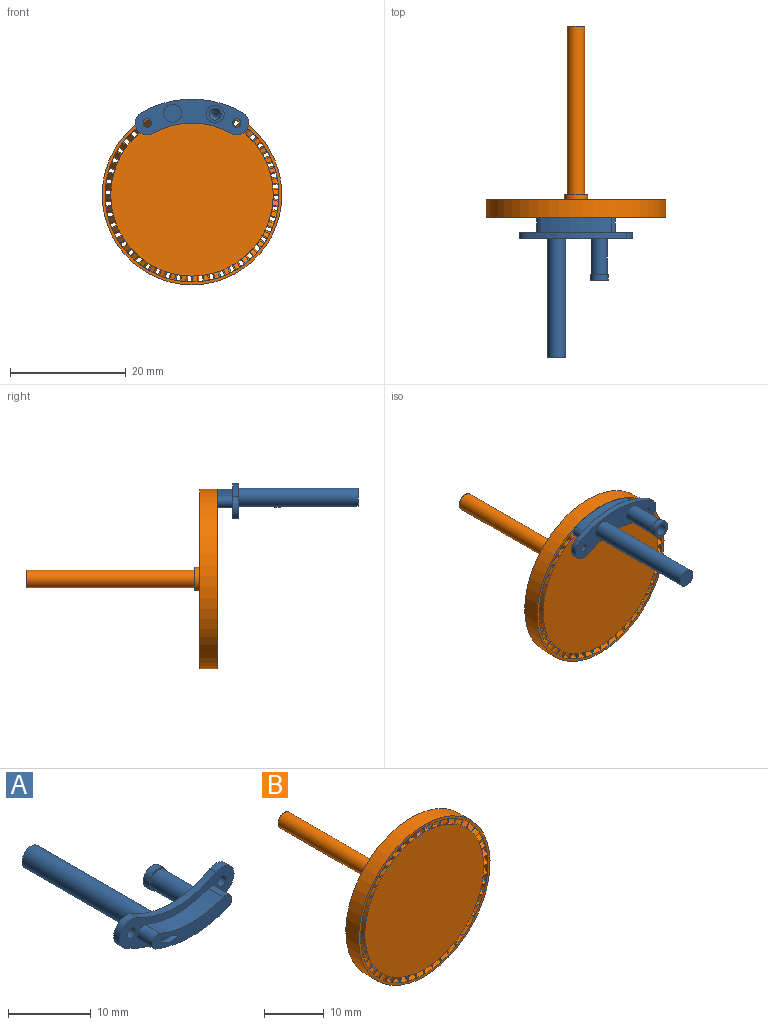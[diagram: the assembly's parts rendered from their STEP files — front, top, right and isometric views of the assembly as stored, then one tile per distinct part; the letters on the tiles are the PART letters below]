
ASSEMBLY  parts=2 mates=1
PART A: 22 faces, bbox 19.6x25x6.2 mm
  f0: cylinder r=1.54mm len=20.6mm, axis (0,-1,0), area 200mm2, adj f16,f21
  f1: cone r=0.41mm half-angle=45deg, axis (0,1,0), area 4mm2, adj f2,f5
  f2: bspline ~9.82x4.39mm, area 23.5mm2, adj f1,f12
  f3: cylinder r=1.03mm len=2.58mm, axis (0,1,0), area 8.3mm2, adj f12,f13,f19,f20
  f4: cylinder r=1.03mm len=2.58mm, axis (0,1,0), area 8.3mm2, adj f12,f13,f19,f20
  f5: cylinder r=1.03mm len=6.59mm, axis (0,-1,0), area 42.7mm2, adj f1,f17
  f6: cylinder r=1.54mm len=3.09mm, axis (0,-1,0), area 10mm2, adj f17,f18
  f7: cylinder r=1.39mm len=6.18mm, axis (0,-1,0), area 54mm2, adj f16,f18
  f8: cylinder r=0.72mm len=1.44mm, axis (0,1,0), area 4.7mm2, adj f13,f16
  f9: cylinder r=0.72mm len=1.44mm, axis (0,1,0), area 4.7mm2, adj f13,f16
  f10: cylinder r=13.39mm len=13.39mm, axis (0,-1,0), area 14.4mm2, adj f13,f14,f15,f16
  f11: cylinder r=17.51mm len=17.51mm, axis (0,-1,0), area 18.9mm2, adj f13,f14,f15,f16
  f12: plane 13.64x3.19mm, normal (0,-1,0), area 25.9mm2, adj f2,f3,f4,f19,f20
  f13: plane 19.57x6.19mm, normal (0,-1,0), area 48.9mm2, adj f3,f4,f8,f9,f10,f11,f14,f15
  f14: cylinder r=2.06mm len=3.84mm, axis (0,-1,0), area 6.7mm2, adj f10,f11,f13,f16
  f15: cylinder r=2.06mm len=3.84mm, axis (0,-1,0), area 6.7mm2, adj f10,f11,f13,f16
  f16: plane 19.57x6.19mm, normal (0,1,0), area 63.2mm2, adj f0,f7,f8,f9,f10,f11,f14,f15
  f17: plane 3.09x3.09mm, normal (0,1,0), area 4.2mm2, adj f5,f6
  f18: plane 3.09x3.09mm, normal (0,-1,0), area 1.4mm2, adj f6,f7
  f19: cylinder r=16.48mm len=12.35mm, axis (0,1,0), area 32.6mm2, adj f3,f4,f12,f13
  f20: cylinder r=14.42mm len=10.8mm, axis (0,1,0), area 28.5mm2, adj f3,f4,f12,f13
  f21: plane 3.09x3.09mm, normal (0,1,0), area 7.5mm2, adj f0
PART B: 295 faces, bbox 31x33x31 mm
  f0: cylinder r=2.02mm len=3mm, axis (0,0,-1), area 3.4mm2, adj f192,f240,f241,f289
  f1: plane 1.03x0.8mm, normal (-0.71,0.7,0), area 1.1mm2, adj f2,f239,f240,f242
  f2: cylinder r=1mm len=1.4mm, axis (0,0,-1), area 1.6mm2, adj f1,f3,f239,f242
  f3: plane 1.03x0.8mm, normal (-0.72,-0.7,0), area 1.1mm2, adj f2,f239,f241,f242
  f4: cylinder r=2.02mm len=3mm, axis (0.13,0,-0.99), area 3.4mm2, adj f239,f240,f241,f242
  f5: plane 1.12x0.91mm, normal (-0.7,0.7,-0.09), area 1.1mm2, adj f6,f238,f240,f243
  f6: cylinder r=1mm len=1.4mm, axis (0.13,0,-0.99), area 1.6mm2, adj f5,f7,f238,f243
  f7: plane 1.12x0.9mm, normal (-0.71,-0.7,-0.09), area 1.1mm2, adj f6,f238,f241,f243
  f8: cylinder r=2.02mm len=3mm, axis (0.26,0,-0.97), area 3.4mm2, adj f238,f240,f241,f243
  f9: plane 1.2x1.01mm, normal (-0.69,0.7,-0.18), area 1.1mm2, adj f10,f237,f240,f244
  f10: cylinder r=1mm len=1.4mm, axis (0.26,0,-0.97), area 1.6mm2, adj f9,f11,f237,f244
  f11: plane 1.19x1.01mm, normal (-0.69,-0.7,-0.19), area 1.1mm2, adj f10,f237,f241,f244
  f12: cylinder r=2.02mm len=3mm, axis (0.38,0,-0.92), area 3.4mm2, adj f237,f240,f241,f244
  f13: plane 1.25x1.1mm, normal (-0.66,0.7,-0.27), area 1.1mm2, adj f14,f236,f240,f245
  f14: cylinder r=1mm len=1.4mm, axis (0.38,0,-0.92), area 1.6mm2, adj f13,f15,f236,f245
  f15: plane 1.25x1.1mm, normal (-0.66,-0.7,-0.27), area 1.1mm2, adj f14,f236,f241,f245
  f16: cylinder r=2.02mm len=3mm, axis (0.5,0,-0.87), area 3.4mm2, adj f236,f240,f241,f245
  f17: plane 1.28x1.17mm, normal (-0.62,0.7,-0.36), area 1.1mm2, adj f18,f235,f240,f246
  f18: cylinder r=1mm len=1.4mm, axis (0.5,0,-0.87), area 1.6mm2, adj f17,f19,f235,f246
  f19: plane 1.28x1.16mm, normal (-0.62,-0.7,-0.36), area 1.1mm2, adj f18,f235,f241,f246
  f20: cylinder r=2.02mm len=3mm, axis (0.61,0,-0.79), area 3.4mm2, adj f235,f240,f241,f246
  f21: plane 1.29x1.22mm, normal (-0.56,0.7,-0.43), area 1.1mm2, adj f22,f234,f240,f247
  f22: cylinder r=1mm len=1.4mm, axis (0.61,0,-0.79), area 1.6mm2, adj f21,f23,f234,f247
  f23: plane 1.29x1.21mm, normal (-0.57,-0.7,-0.44), area 1.1mm2, adj f22,f234,f241,f247
  f24: cylinder r=2.02mm len=3mm, axis (0.71,0,-0.71), area 3.4mm2, adj f234,f240,f241,f247
  f25: plane 1.28x1.25mm, normal (-0.5,0.7,-0.5), area 1.1mm2, adj f26,f233,f240,f248
  f26: cylinder r=1mm len=1.4mm, axis (0.71,0,-0.71), area 1.6mm2, adj f25,f27,f233,f248
  f27: plane 1.28x1.24mm, normal (-0.51,-0.7,-0.51), area 1.1mm2, adj f26,f233,f241,f248
  f28: cylinder r=2.02mm len=3mm, axis (0.79,0,-0.61), area 3.4mm2, adj f233,f240,f241,f248
  f29: plane 1.25x1.25mm, normal (-0.43,0.7,-0.56), area 1.1mm2, adj f30,f232,f240,f249
  f30: cylinder r=1mm len=1.4mm, axis (0.79,0,-0.61), area 1.6mm2, adj f29,f31,f232,f249
  f31: plane 1.25x1.25mm, normal (-0.44,-0.7,-0.57), area 1.1mm2, adj f30,f232,f241,f249
  f32: cylinder r=2.02mm len=3mm, axis (0.87,0,-0.5), area 3.4mm2, adj f232,f240,f241,f249
  f33: plane 1.24x1.2mm, normal (-0.36,0.7,-0.62), area 1.1mm2, adj f34,f231,f240,f250
  f34: cylinder r=1mm len=1.4mm, axis (0.87,0,-0.5), area 1.6mm2, adj f33,f35,f231,f250
  f35: plane 1.24x1.19mm, normal (-0.36,-0.7,-0.62), area 1.1mm2, adj f34,f231,f241,f250
  f36: cylinder r=2.02mm len=3mm, axis (0.92,0,-0.38), area 3.4mm2, adj f231,f240,f241,f250
  f37: plane 1.2x1.12mm, normal (-0.27,0.7,-0.66), area 1.1mm2, adj f38,f230,f240,f251
  f38: cylinder r=1mm len=1.4mm, axis (0.92,0,-0.38), area 1.6mm2, adj f37,f39,f230,f251
  f39: plane 1.2x1.12mm, normal (-0.27,-0.7,-0.66), area 1.1mm2, adj f38,f230,f241,f251
  f40: cylinder r=2.02mm len=3mm, axis (0.97,0,-0.26), area 3.4mm2, adj f230,f240,f241,f251
  f41: plane 1.15x1.03mm, normal (-0.18,0.7,-0.69), area 1.1mm2, adj f42,f229,f240,f252
  f42: cylinder r=1mm len=1.4mm, axis (0.97,0,-0.26), area 1.6mm2, adj f41,f43,f229,f252
  f43: plane 1.14x1.02mm, normal (-0.19,-0.7,-0.69), area 1.1mm2, adj f42,f229,f241,f252
  f44: cylinder r=2.02mm len=3mm, axis (0.99,0,-0.13), area 3.4mm2, adj f229,f240,f241,f252
  f45: plane 1.07x0.92mm, normal (-0.09,0.7,-0.7), area 1.1mm2, adj f46,f228,f240,f253
  f46: cylinder r=1mm len=1.4mm, axis (0.99,0,-0.13), area 1.6mm2, adj f45,f47,f228,f253
  f47: plane 1.07x0.91mm, normal (-0.09,-0.7,-0.71), area 1.1mm2, adj f46,f228,f241,f253
  f48: cylinder r=2.02mm len=3mm, axis (1,0,0), area 3.4mm2, adj f228,f240,f241,f253
  f49: plane 1.03x0.8mm, normal (0,0.7,-0.71), area 1.1mm2, adj f50,f227,f240,f254
  f50: cylinder r=1mm len=1.4mm, axis (1,0,0), area 1.6mm2, adj f49,f51,f227,f254
  f51: plane 1.03x0.8mm, normal (0,-0.7,-0.72), area 1.1mm2, adj f50,f227,f241,f254
  f52: cylinder r=2.02mm len=3mm, axis (0.99,0,0.13), area 3.4mm2, adj f227,f240,f241,f254
  f53: plane 1.12x0.91mm, normal (0.09,0.7,-0.7), area 1.1mm2, adj f54,f226,f240,f255
  f54: cylinder r=1mm len=1.4mm, axis (0.99,0,0.13), area 1.6mm2, adj f53,f55,f226,f255
  f55: plane 1.12x0.9mm, normal (0.09,-0.7,-0.71), area 1.1mm2, adj f54,f226,f241,f255
  f56: cylinder r=2.02mm len=3mm, axis (0.97,0,0.26), area 3.4mm2, adj f226,f240,f241,f255
  f57: plane 1.2x1.01mm, normal (0.18,0.7,-0.69), area 1.1mm2, adj f58,f225,f240,f256
  f58: cylinder r=1mm len=1.4mm, axis (0.97,0,0.26), area 1.6mm2, adj f57,f59,f225,f256
  f59: plane 1.19x1.01mm, normal (0.19,-0.7,-0.69), area 1.1mm2, adj f58,f225,f241,f256
  f60: cylinder r=2.02mm len=3mm, axis (0.92,0,0.38), area 3.4mm2, adj f225,f240,f241,f256
  f61: plane 1.25x1.1mm, normal (0.27,0.7,-0.66), area 1.1mm2, adj f62,f224,f240,f257
  f62: cylinder r=1mm len=1.4mm, axis (0.92,0,0.38), area 1.6mm2, adj f61,f63,f224,f257
  f63: plane 1.25x1.1mm, normal (0.27,-0.7,-0.66), area 1.1mm2, adj f62,f224,f241,f257
  f64: cylinder r=2.02mm len=3mm, axis (0.87,0,0.5), area 3.4mm2, adj f224,f240,f241,f257
  f65: plane 1.28x1.17mm, normal (0.36,0.7,-0.62), area 1.1mm2, adj f66,f223,f240,f258
  f66: cylinder r=1mm len=1.4mm, axis (0.87,0,0.5), area 1.6mm2, adj f65,f67,f223,f258
  f67: plane 1.28x1.16mm, normal (0.36,-0.7,-0.62), area 1.1mm2, adj f66,f223,f241,f258
  f68: cylinder r=2.02mm len=3mm, axis (0.79,0,0.61), area 3.4mm2, adj f223,f240,f241,f258
  f69: plane 1.29x1.22mm, normal (0.43,0.7,-0.56), area 1.1mm2, adj f70,f222,f240,f259
  f70: cylinder r=1mm len=1.4mm, axis (0.79,0,0.61), area 1.6mm2, adj f69,f71,f222,f259
  f71: plane 1.29x1.21mm, normal (0.44,-0.7,-0.57), area 1.1mm2, adj f70,f222,f241,f259
  f72: cylinder r=2.02mm len=3mm, axis (0.71,0,0.71), area 3.4mm2, adj f222,f240,f241,f259
  f73: plane 1.28x1.25mm, normal (0.5,0.7,-0.5), area 1.1mm2, adj f74,f221,f240,f260
  f74: cylinder r=1mm len=1.4mm, axis (0.71,0,0.71), area 1.6mm2, adj f73,f75,f221,f260
  f75: plane 1.28x1.24mm, normal (0.51,-0.7,-0.51), area 1.1mm2, adj f74,f221,f241,f260
  f76: cylinder r=2.02mm len=3mm, axis (0.61,0,0.79), area 3.4mm2, adj f221,f240,f241,f260
  f77: plane 1.25x1.25mm, normal (0.56,0.7,-0.43), area 1.1mm2, adj f78,f220,f240,f261
  f78: cylinder r=1mm len=1.4mm, axis (0.61,0,0.79), area 1.6mm2, adj f77,f79,f220,f261
  f79: plane 1.25x1.25mm, normal (0.57,-0.7,-0.44), area 1.1mm2, adj f78,f220,f241,f261
  f80: cylinder r=2.02mm len=3mm, axis (0.5,0,0.87), area 3.4mm2, adj f220,f240,f241,f261
  f81: plane 1.24x1.2mm, normal (0.62,0.7,-0.36), area 1.1mm2, adj f82,f219,f240,f262
  f82: cylinder r=1mm len=1.4mm, axis (0.5,0,0.87), area 1.6mm2, adj f81,f83,f219,f262
  f83: plane 1.24x1.19mm, normal (0.62,-0.7,-0.36), area 1.1mm2, adj f82,f219,f241,f262
  f84: cylinder r=2.02mm len=3mm, axis (0.38,0,0.92), area 3.4mm2, adj f219,f240,f241,f262
  f85: plane 1.2x1.12mm, normal (0.66,0.7,-0.27), area 1.1mm2, adj f86,f218,f240,f263
  f86: cylinder r=1mm len=1.4mm, axis (0.38,0,0.92), area 1.6mm2, adj f85,f87,f218,f263
  f87: plane 1.2x1.12mm, normal (0.66,-0.7,-0.27), area 1.1mm2, adj f86,f218,f241,f263
  f88: cylinder r=2.02mm len=3mm, axis (0.26,0,0.97), area 3.4mm2, adj f218,f240,f241,f263
  f89: plane 1.15x1.03mm, normal (0.69,0.7,-0.18), area 1.1mm2, adj f90,f217,f240,f264
  f90: cylinder r=1mm len=1.4mm, axis (0.26,0,0.97), area 1.6mm2, adj f89,f91,f217,f264
  f91: plane 1.14x1.02mm, normal (0.69,-0.7,-0.19), area 1.1mm2, adj f90,f217,f241,f264
  f92: cylinder r=2.02mm len=3mm, axis (0.13,0,0.99), area 3.4mm2, adj f217,f240,f241,f264
  f93: plane 1.07x0.92mm, normal (0.7,0.7,-0.09), area 1.1mm2, adj f94,f216,f240,f265
  f94: cylinder r=1mm len=1.4mm, axis (0.13,0,0.99), area 1.6mm2, adj f93,f95,f216,f265
  f95: plane 1.07x0.91mm, normal (0.71,-0.7,-0.09), area 1.1mm2, adj f94,f216,f241,f265
  f96: cylinder r=2.02mm len=3mm, axis (0,0,1), area 3.4mm2, adj f216,f240,f241,f265
  f97: plane 1.03x0.8mm, normal (0.71,0.7,0), area 1.1mm2, adj f98,f215,f240,f266
  f98: cylinder r=1mm len=1.4mm, axis (0,0,1), area 1.6mm2, adj f97,f99,f215,f266
  f99: plane 1.03x0.8mm, normal (0.72,-0.7,0), area 1.1mm2, adj f98,f215,f241,f266
  f100: cylinder r=2.02mm len=3mm, axis (-0.13,0,0.99), area 3.4mm2, adj f215,f240,f241,f266
  f101: plane 1.12x0.91mm, normal (0.7,0.7,0.09), area 1.1mm2, adj f102,f214,f240,f267
  f102: cylinder r=1mm len=1.4mm, axis (-0.13,0,0.99), area 1.6mm2, adj f101,f103,f214,f267
  f103: plane 1.12x0.9mm, normal (0.71,-0.7,0.09), area 1.1mm2, adj f102,f214,f241,f267
  f104: cylinder r=2.02mm len=3mm, axis (-0.26,0,0.97), area 3.4mm2, adj f214,f240,f241,f267
  f105: plane 1.2x1.01mm, normal (0.69,0.7,0.18), area 1.1mm2, adj f106,f213,f240,f268
  f106: cylinder r=1mm len=1.4mm, axis (-0.26,0,0.97), area 1.6mm2, adj f105,f107,f213,f268
  f107: plane 1.19x1.01mm, normal (0.69,-0.7,0.19), area 1.1mm2, adj f106,f213,f241,f268
  f108: cylinder r=2.02mm len=3mm, axis (-0.38,0,0.92), area 3.4mm2, adj f213,f240,f241,f268
  f109: plane 1.25x1.1mm, normal (0.66,0.7,0.27), area 1.1mm2, adj f110,f212,f240,f269
  f110: cylinder r=1mm len=1.4mm, axis (-0.38,0,0.92), area 1.6mm2, adj f109,f111,f212,f269
  f111: plane 1.25x1.1mm, normal (0.66,-0.7,0.27), area 1.1mm2, adj f110,f212,f241,f269
  f112: cylinder r=2.02mm len=3mm, axis (-0.5,0,0.87), area 3.4mm2, adj f212,f240,f241,f269
  f113: plane 1.28x1.17mm, normal (0.62,0.7,0.36), area 1.1mm2, adj f114,f211,f240,f270
  f114: cylinder r=1mm len=1.4mm, axis (-0.5,0,0.87), area 1.6mm2, adj f113,f115,f211,f270
  f115: plane 1.28x1.16mm, normal (0.62,-0.7,0.36), area 1.1mm2, adj f114,f211,f241,f270
  f116: cylinder r=2.02mm len=3mm, axis (-0.61,0,0.79), area 3.4mm2, adj f211,f240,f241,f270
  f117: plane 1.29x1.22mm, normal (0.56,0.7,0.43), area 1.1mm2, adj f118,f210,f240,f271
  f118: cylinder r=1mm len=1.4mm, axis (-0.61,0,0.79), area 1.6mm2, adj f117,f119,f210,f271
  f119: plane 1.29x1.21mm, normal (0.57,-0.7,0.44), area 1.1mm2, adj f118,f210,f241,f271
  f120: cylinder r=2.02mm len=3mm, axis (-0.71,0,0.71), area 3.4mm2, adj f210,f240,f241,f271
  f121: plane 1.28x1.25mm, normal (0.5,0.7,0.5), area 1.1mm2, adj f122,f209,f240,f272
  f122: cylinder r=1mm len=1.4mm, axis (-0.71,0,0.71), area 1.6mm2, adj f121,f123,f209,f272
  f123: plane 1.28x1.24mm, normal (0.51,-0.7,0.51), area 1.1mm2, adj f122,f209,f241,f272
  f124: cylinder r=2.02mm len=3mm, axis (-0.79,0,0.61), area 3.4mm2, adj f209,f240,f241,f272
  f125: plane 1.25x1.25mm, normal (0.43,0.7,0.56), area 1.1mm2, adj f126,f208,f240,f273
  f126: cylinder r=1mm len=1.4mm, axis (-0.79,0,0.61), area 1.6mm2, adj f125,f127,f208,f273
  f127: plane 1.25x1.25mm, normal (0.44,-0.7,0.57), area 1.1mm2, adj f126,f208,f241,f273
  f128: cylinder r=2.02mm len=3mm, axis (-0.87,0,0.5), area 3.4mm2, adj f208,f240,f241,f273
  f129: plane 1.24x1.2mm, normal (0.36,0.7,0.62), area 1.1mm2, adj f130,f207,f240,f274
  f130: cylinder r=1mm len=1.4mm, axis (-0.87,0,0.5), area 1.6mm2, adj f129,f131,f207,f274
  f131: plane 1.24x1.19mm, normal (0.36,-0.7,0.62), area 1.1mm2, adj f130,f207,f241,f274
  f132: cylinder r=2.02mm len=3mm, axis (-0.92,0,0.38), area 3.4mm2, adj f207,f240,f241,f274
  f133: plane 1.2x1.12mm, normal (0.27,0.7,0.66), area 1.1mm2, adj f134,f206,f240,f275
  f134: cylinder r=1mm len=1.4mm, axis (-0.92,0,0.38), area 1.6mm2, adj f133,f135,f206,f275
  f135: plane 1.2x1.12mm, normal (0.27,-0.7,0.66), area 1.1mm2, adj f134,f206,f241,f275
  f136: cylinder r=2.02mm len=3mm, axis (-0.97,0,0.26), area 3.4mm2, adj f206,f240,f241,f275
  f137: plane 1.15x1.03mm, normal (0.18,0.7,0.69), area 1.1mm2, adj f138,f205,f240,f276
  f138: cylinder r=1mm len=1.4mm, axis (-0.97,0,0.26), area 1.6mm2, adj f137,f139,f205,f276
  f139: plane 1.14x1.02mm, normal (0.19,-0.7,0.69), area 1.1mm2, adj f138,f205,f241,f276
  f140: cylinder r=2.02mm len=3mm, axis (-0.99,0,0.13), area 3.4mm2, adj f205,f240,f241,f276
  f141: plane 1.07x0.92mm, normal (0.09,0.7,0.7), area 1.1mm2, adj f142,f204,f240,f277
  f142: cylinder r=1mm len=1.4mm, axis (-0.99,0,0.13), area 1.6mm2, adj f141,f143,f204,f277
  f143: plane 1.07x0.91mm, normal (0.09,-0.7,0.71), area 1.1mm2, adj f142,f204,f241,f277
  f144: cylinder r=2.02mm len=3mm, axis (-1,0,0), area 3.4mm2, adj f204,f240,f241,f277
  f145: plane 1.03x0.8mm, normal (0,0.7,0.71), area 1.1mm2, adj f146,f203,f240,f278
  f146: cylinder r=1mm len=1.4mm, axis (-1,0,0), area 1.6mm2, adj f145,f147,f203,f278
  f147: plane 1.03x0.8mm, normal (0,-0.7,0.72), area 1.1mm2, adj f146,f203,f241,f278
  f148: cylinder r=2.02mm len=3mm, axis (-0.99,0,-0.13), area 3.4mm2, adj f203,f240,f241,f278
  f149: plane 1.12x0.91mm, normal (-0.09,0.7,0.7), area 1.1mm2, adj f150,f202,f240,f279
  f150: cylinder r=1mm len=1.4mm, axis (-0.99,0,-0.13), area 1.6mm2, adj f149,f151,f202,f279
  f151: plane 1.12x0.9mm, normal (-0.09,-0.7,0.71), area 1.1mm2, adj f150,f202,f241,f279
  f152: cylinder r=2.02mm len=3mm, axis (-0.97,0,-0.26), area 3.4mm2, adj f202,f240,f241,f279
  f153: plane 1.2x1.01mm, normal (-0.18,0.7,0.69), area 1.1mm2, adj f154,f201,f240,f280
  f154: cylinder r=1mm len=1.4mm, axis (-0.97,0,-0.26), area 1.6mm2, adj f153,f155,f201,f280
  f155: plane 1.19x1.01mm, normal (-0.19,-0.7,0.69), area 1.1mm2, adj f154,f201,f241,f280
  f156: cylinder r=2.02mm len=3mm, axis (-0.92,0,-0.38), area 3.4mm2, adj f201,f240,f241,f280
  f157: plane 1.25x1.1mm, normal (-0.27,0.7,0.66), area 1.1mm2, adj f158,f200,f240,f281
  f158: cylinder r=1mm len=1.4mm, axis (-0.92,0,-0.38), area 1.6mm2, adj f157,f159,f200,f281
  f159: plane 1.25x1.1mm, normal (-0.27,-0.7,0.66), area 1.1mm2, adj f158,f200,f241,f281
  f160: cylinder r=2.02mm len=3mm, axis (-0.87,0,-0.5), area 3.4mm2, adj f200,f240,f241,f281
  f161: plane 1.28x1.17mm, normal (-0.36,0.7,0.62), area 1.1mm2, adj f162,f199,f240,f282
  f162: cylinder r=1mm len=1.4mm, axis (-0.87,0,-0.5), area 1.6mm2, adj f161,f163,f199,f282
  f163: plane 1.28x1.16mm, normal (-0.36,-0.7,0.62), area 1.1mm2, adj f162,f199,f241,f282
  f164: cylinder r=2.02mm len=3mm, axis (-0.79,0,-0.61), area 3.4mm2, adj f199,f240,f241,f282
  f165: plane 1.29x1.22mm, normal (-0.43,0.7,0.56), area 1.1mm2, adj f166,f198,f240,f283
  f166: cylinder r=1mm len=1.4mm, axis (-0.79,0,-0.61), area 1.6mm2, adj f165,f167,f198,f283
  f167: plane 1.29x1.21mm, normal (-0.44,-0.7,0.57), area 1.1mm2, adj f166,f198,f241,f283
  f168: cylinder r=2.02mm len=3mm, axis (-0.71,0,-0.71), area 3.4mm2, adj f198,f240,f241,f283
  f169: plane 1.28x1.25mm, normal (-0.5,0.7,0.5), area 1.1mm2, adj f170,f197,f240,f284
  f170: cylinder r=1mm len=1.4mm, axis (-0.71,0,-0.71), area 1.6mm2, adj f169,f171,f197,f284
  f171: plane 1.28x1.24mm, normal (-0.51,-0.7,0.51), area 1.1mm2, adj f170,f197,f241,f284
  f172: cylinder r=2.02mm len=3mm, axis (-0.61,0,-0.79), area 3.4mm2, adj f197,f240,f241,f284
  f173: plane 1.25x1.25mm, normal (-0.56,0.7,0.43), area 1.1mm2, adj f174,f196,f240,f285
  f174: cylinder r=1mm len=1.4mm, axis (-0.61,0,-0.79), area 1.6mm2, adj f173,f175,f196,f285
  f175: plane 1.25x1.25mm, normal (-0.57,-0.7,0.44), area 1.1mm2, adj f174,f196,f241,f285
  f176: cylinder r=2.02mm len=3mm, axis (-0.5,0,-0.87), area 3.4mm2, adj f196,f240,f241,f285
  f177: plane 1.24x1.2mm, normal (-0.62,0.7,0.36), area 1.1mm2, adj f178,f195,f240,f286
  f178: cylinder r=1mm len=1.4mm, axis (-0.5,0,-0.87), area 1.6mm2, adj f177,f179,f195,f286
  f179: plane 1.24x1.19mm, normal (-0.62,-0.7,0.36), area 1.1mm2, adj f178,f195,f241,f286
  f180: cylinder r=2.02mm len=3mm, axis (-0.38,0,-0.92), area 3.4mm2, adj f195,f240,f241,f286
  f181: plane 1.2x1.12mm, normal (-0.66,0.7,0.27), area 1.1mm2, adj f182,f194,f240,f287
  f182: cylinder r=1mm len=1.4mm, axis (-0.38,0,-0.92), area 1.6mm2, adj f181,f183,f194,f287
  f183: plane 1.2x1.12mm, normal (-0.66,-0.7,0.27), area 1.1mm2, adj f182,f194,f241,f287
  f184: cylinder r=2.02mm len=3mm, axis (-0.26,0,-0.97), area 3.4mm2, adj f194,f240,f241,f287
  f185: plane 1.15x1.03mm, normal (-0.69,0.7,0.18), area 1.1mm2, adj f186,f193,f240,f288
  f186: cylinder r=1mm len=1.4mm, axis (-0.26,0,-0.97), area 1.6mm2, adj f185,f187,f193,f288
  f187: plane 1.14x1.02mm, normal (-0.69,-0.7,0.19), area 1.1mm2, adj f186,f193,f241,f288
  f188: cylinder r=2.02mm len=3mm, axis (-0.13,0,-0.99), area 3.4mm2, adj f193,f240,f241,f288
  f189: plane 1.07x0.92mm, normal (-0.7,0.7,0.09), area 1.1mm2, adj f190,f192,f240,f289
  f190: cylinder r=1mm len=1.4mm, axis (-0.13,0,-0.99), area 1.6mm2, adj f189,f191,f192,f289
  f191: plane 1.07x0.91mm, normal (-0.71,-0.7,0.09), area 1.1mm2, adj f190,f192,f241,f289
  f192: cylinder r=14mm len=3mm, axis (0,-1,0), area 4.4mm2, adj f0,f189,f190,f191,f240,f241
  f193: cylinder r=14mm len=3mm, axis (0,-1,0), area 4.4mm2, adj f185,f186,f187,f188,f240,f241
  f194: cylinder r=14mm len=3mm, axis (0,-1,0), area 4.4mm2, adj f181,f182,f183,f184,f240,f241
  f195: cylinder r=14mm len=3mm, axis (0,-1,0), area 4.4mm2, adj f177,f178,f179,f180,f240,f241
  f196: cylinder r=14mm len=3mm, axis (0,-1,0), area 4.4mm2, adj f173,f174,f175,f176,f240,f241
  f197: cylinder r=14mm len=3mm, axis (0,-1,0), area 4.4mm2, adj f169,f170,f171,f172,f240,f241
  f198: cylinder r=14mm len=3mm, axis (0,-1,0), area 4.4mm2, adj f165,f166,f167,f168,f240,f241
  f199: cylinder r=14mm len=3mm, axis (0,-1,0), area 4.4mm2, adj f161,f162,f163,f164,f240,f241
  f200: cylinder r=14mm len=3mm, axis (0,-1,0), area 4.4mm2, adj f157,f158,f159,f160,f240,f241
  f201: cylinder r=14mm len=3mm, axis (0,-1,0), area 4.4mm2, adj f153,f154,f155,f156,f240,f241
  f202: cylinder r=14mm len=3mm, axis (0,-1,0), area 4.4mm2, adj f149,f150,f151,f152,f240,f241
  f203: cylinder r=14mm len=3mm, axis (0,-1,0), area 4.4mm2, adj f145,f146,f147,f148,f240,f241
  f204: cylinder r=14mm len=3mm, axis (0,-1,0), area 4.4mm2, adj f141,f142,f143,f144,f240,f241
  f205: cylinder r=14mm len=3mm, axis (0,-1,0), area 4.4mm2, adj f137,f138,f139,f140,f240,f241
  f206: cylinder r=14mm len=3mm, axis (0,-1,0), area 4.4mm2, adj f133,f134,f135,f136,f240,f241
  f207: cylinder r=14mm len=3mm, axis (0,-1,0), area 4.4mm2, adj f129,f130,f131,f132,f240,f241
  f208: cylinder r=14mm len=3mm, axis (0,-1,0), area 4.4mm2, adj f125,f126,f127,f128,f240,f241
  f209: cylinder r=14mm len=3mm, axis (0,-1,0), area 4.4mm2, adj f121,f122,f123,f124,f240,f241
  f210: cylinder r=14mm len=3mm, axis (0,-1,0), area 4.4mm2, adj f117,f118,f119,f120,f240,f241
  f211: cylinder r=14mm len=3mm, axis (0,-1,0), area 4.4mm2, adj f113,f114,f115,f116,f240,f241
  f212: cylinder r=14mm len=3mm, axis (0,-1,0), area 4.4mm2, adj f109,f110,f111,f112,f240,f241
  f213: cylinder r=14mm len=3mm, axis (0,-1,0), area 4.4mm2, adj f105,f106,f107,f108,f240,f241
  f214: cylinder r=14mm len=3mm, axis (0,-1,0), area 4.4mm2, adj f101,f102,f103,f104,f240,f241
  f215: cylinder r=14mm len=3mm, axis (0,-1,0), area 4.4mm2, adj f97,f98,f99,f100,f240,f241
  f216: cylinder r=14mm len=3mm, axis (0,-1,0), area 4.4mm2, adj f93,f94,f95,f96,f240,f241
  f217: cylinder r=14mm len=3mm, axis (0,-1,0), area 4.4mm2, adj f89,f90,f91,f92,f240,f241
  f218: cylinder r=14mm len=3mm, axis (0,-1,0), area 4.4mm2, adj f85,f86,f87,f88,f240,f241
  f219: cylinder r=14mm len=3mm, axis (0,-1,0), area 4.4mm2, adj f81,f82,f83,f84,f240,f241
  f220: cylinder r=14mm len=3mm, axis (0,-1,0), area 4.4mm2, adj f77,f78,f79,f80,f240,f241
  f221: cylinder r=14mm len=3mm, axis (0,-1,0), area 4.4mm2, adj f73,f74,f75,f76,f240,f241
  f222: cylinder r=14mm len=3mm, axis (0,-1,0), area 4.4mm2, adj f69,f70,f71,f72,f240,f241
  f223: cylinder r=14mm len=3mm, axis (0,-1,0), area 4.4mm2, adj f65,f66,f67,f68,f240,f241
  f224: cylinder r=14mm len=3mm, axis (0,-1,0), area 4.4mm2, adj f61,f62,f63,f64,f240,f241
  f225: cylinder r=14mm len=3mm, axis (0,-1,0), area 4.4mm2, adj f57,f58,f59,f60,f240,f241
  f226: cylinder r=14mm len=3mm, axis (0,-1,0), area 4.4mm2, adj f53,f54,f55,f56,f240,f241
  f227: cylinder r=14mm len=3mm, axis (0,-1,0), area 4.4mm2, adj f49,f50,f51,f52,f240,f241
  f228: cylinder r=14mm len=3mm, axis (0,-1,0), area 4.4mm2, adj f45,f46,f47,f48,f240,f241
  f229: cylinder r=14mm len=3mm, axis (0,-1,0), area 4.4mm2, adj f41,f42,f43,f44,f240,f241
  f230: cylinder r=14mm len=3mm, axis (0,-1,0), area 4.4mm2, adj f37,f38,f39,f40,f240,f241
  f231: cylinder r=14mm len=3mm, axis (0,-1,0), area 4.4mm2, adj f33,f34,f35,f36,f240,f241
  f232: cylinder r=14mm len=3mm, axis (0,-1,0), area 4.4mm2, adj f29,f30,f31,f32,f240,f241
  f233: cylinder r=14mm len=3mm, axis (0,-1,0), area 4.4mm2, adj f25,f26,f27,f28,f240,f241
  f234: cylinder r=14mm len=3mm, axis (0,-1,0), area 4.4mm2, adj f21,f22,f23,f24,f240,f241
  f235: cylinder r=14mm len=3mm, axis (0,-1,0), area 4.4mm2, adj f17,f18,f19,f20,f240,f241
  f236: cylinder r=14mm len=3mm, axis (0,-1,0), area 4.4mm2, adj f13,f14,f15,f16,f240,f241
  f237: cylinder r=14mm len=3mm, axis (0,-1,0), area 4.4mm2, adj f9,f10,f11,f12,f240,f241
  f238: cylinder r=14mm len=3mm, axis (0,-1,0), area 4.4mm2, adj f5,f6,f7,f8,f240,f241
  f239: cylinder r=14mm len=3mm, axis (0,-1,0), area 4.4mm2, adj f1,f2,f3,f4,f240,f241
  f240: plane 31x31mm, normal (0,1,0), area 659.2mm2, adj f0,f1,f4,f5,f8,f9,f12,f13
  f241: plane 31x31mm, normal (0,-1,0), area 672.4mm2, adj f0,f3,f4,f7,f8,f11,f12,f15
  f242: cylinder r=15mm len=3mm, axis (0,-1,0), area 4.7mm2, adj f1,f2,f3,f4,f240,f241
  f243: cylinder r=15mm len=3mm, axis (0,-1,0), area 4.7mm2, adj f5,f6,f7,f8,f240,f241
  f244: cylinder r=15mm len=3mm, axis (0,-1,0), area 4.7mm2, adj f9,f10,f11,f12,f240,f241
  f245: cylinder r=15mm len=3mm, axis (0,-1,0), area 4.7mm2, adj f13,f14,f15,f16,f240,f241
  f246: cylinder r=15mm len=3mm, axis (0,-1,0), area 4.7mm2, adj f17,f18,f19,f20,f240,f241
  f247: cylinder r=15mm len=3mm, axis (0,-1,0), area 4.7mm2, adj f21,f22,f23,f24,f240,f241
  f248: cylinder r=15mm len=3mm, axis (0,-1,0), area 4.7mm2, adj f25,f26,f27,f28,f240,f241
  f249: cylinder r=15mm len=3mm, axis (0,-1,0), area 4.7mm2, adj f29,f30,f31,f32,f240,f241
  f250: cylinder r=15mm len=3mm, axis (0,-1,0), area 4.7mm2, adj f33,f34,f35,f36,f240,f241
  f251: cylinder r=15mm len=3mm, axis (0,-1,0), area 4.7mm2, adj f37,f38,f39,f40,f240,f241
  f252: cylinder r=15mm len=3mm, axis (0,-1,0), area 4.7mm2, adj f41,f42,f43,f44,f240,f241
  f253: cylinder r=15mm len=3mm, axis (0,-1,0), area 4.7mm2, adj f45,f46,f47,f48,f240,f241
  f254: cylinder r=15mm len=3mm, axis (0,-1,0), area 4.7mm2, adj f49,f50,f51,f52,f240,f241
  f255: cylinder r=15mm len=3mm, axis (0,-1,0), area 4.7mm2, adj f53,f54,f55,f56,f240,f241
  f256: cylinder r=15mm len=3mm, axis (0,-1,0), area 4.7mm2, adj f57,f58,f59,f60,f240,f241
  f257: cylinder r=15mm len=3mm, axis (0,-1,0), area 4.7mm2, adj f61,f62,f63,f64,f240,f241
  f258: cylinder r=15mm len=3mm, axis (0,-1,0), area 4.7mm2, adj f65,f66,f67,f68,f240,f241
  f259: cylinder r=15mm len=3mm, axis (0,-1,0), area 4.7mm2, adj f69,f70,f71,f72,f240,f241
  f260: cylinder r=15mm len=3mm, axis (0,-1,0), area 4.7mm2, adj f73,f74,f75,f76,f240,f241
  f261: cylinder r=15mm len=3mm, axis (0,-1,0), area 4.7mm2, adj f77,f78,f79,f80,f240,f241
  f262: cylinder r=15mm len=3mm, axis (0,-1,0), area 4.7mm2, adj f81,f82,f83,f84,f240,f241
  f263: cylinder r=15mm len=3mm, axis (0,-1,0), area 4.7mm2, adj f85,f86,f87,f88,f240,f241
  f264: cylinder r=15mm len=3mm, axis (0,-1,0), area 4.7mm2, adj f89,f90,f91,f92,f240,f241
  f265: cylinder r=15mm len=3mm, axis (0,-1,0), area 4.7mm2, adj f93,f94,f95,f96,f240,f241
  f266: cylinder r=15mm len=3mm, axis (0,-1,0), area 4.7mm2, adj f97,f98,f99,f100,f240,f241
  f267: cylinder r=15mm len=3mm, axis (0,-1,0), area 4.7mm2, adj f101,f102,f103,f104,f240,f241
  f268: cylinder r=15mm len=3mm, axis (0,-1,0), area 4.7mm2, adj f105,f106,f107,f108,f240,f241
  f269: cylinder r=15mm len=3mm, axis (0,-1,0), area 4.7mm2, adj f109,f110,f111,f112,f240,f241
  f270: cylinder r=15mm len=3mm, axis (0,-1,0), area 4.7mm2, adj f113,f114,f115,f116,f240,f241
  f271: cylinder r=15mm len=3mm, axis (0,-1,0), area 4.7mm2, adj f117,f118,f119,f120,f240,f241
  f272: cylinder r=15mm len=3mm, axis (0,-1,0), area 4.7mm2, adj f121,f122,f123,f124,f240,f241
  f273: cylinder r=15mm len=3mm, axis (0,-1,0), area 4.7mm2, adj f125,f126,f127,f128,f240,f241
  f274: cylinder r=15mm len=3mm, axis (0,-1,0), area 4.7mm2, adj f129,f130,f131,f132,f240,f241
  f275: cylinder r=15mm len=3mm, axis (0,-1,0), area 4.7mm2, adj f133,f134,f135,f136,f240,f241
  f276: cylinder r=15mm len=3mm, axis (0,-1,0), area 4.7mm2, adj f137,f138,f139,f140,f240,f241
  f277: cylinder r=15mm len=3mm, axis (0,-1,0), area 4.7mm2, adj f141,f142,f143,f144,f240,f241
  f278: cylinder r=15mm len=3mm, axis (0,-1,0), area 4.7mm2, adj f145,f146,f147,f148,f240,f241
  f279: cylinder r=15mm len=3mm, axis (0,-1,0), area 4.7mm2, adj f149,f150,f151,f152,f240,f241
  f280: cylinder r=15mm len=3mm, axis (0,-1,0), area 4.7mm2, adj f153,f154,f155,f156,f240,f241
  f281: cylinder r=15mm len=3mm, axis (0,-1,0), area 4.7mm2, adj f157,f158,f159,f160,f240,f241
  f282: cylinder r=15mm len=3mm, axis (0,-1,0), area 4.7mm2, adj f161,f162,f163,f164,f240,f241
  f283: cylinder r=15mm len=3mm, axis (0,-1,0), area 4.7mm2, adj f165,f166,f167,f168,f240,f241
  f284: cylinder r=15mm len=3mm, axis (0,-1,0), area 4.7mm2, adj f169,f170,f171,f172,f240,f241
  f285: cylinder r=15mm len=3mm, axis (0,-1,0), area 4.7mm2, adj f173,f174,f175,f176,f240,f241
  f286: cylinder r=15mm len=3mm, axis (0,-1,0), area 4.7mm2, adj f177,f178,f179,f180,f240,f241
  f287: cylinder r=15mm len=3mm, axis (0,-1,0), area 4.7mm2, adj f181,f182,f183,f184,f240,f241
  f288: cylinder r=15mm len=3mm, axis (0,-1,0), area 4.7mm2, adj f185,f186,f187,f188,f240,f241
  f289: cylinder r=15mm len=3mm, axis (0,-1,0), area 4.7mm2, adj f0,f189,f190,f191,f240,f241
  f290: cylinder r=15.5mm len=31mm, axis (0,-1,0), area 292.2mm2, adj f240,f241
  f291: cylinder r=2mm len=4mm, axis (0,-1,0), area 11.3mm2, adj f240,f292
  f292: plane 4x4mm, normal (0,1,0), area 5.5mm2, adj f291,f294
  f293: plane 3x3mm, normal (0,1,0), area 7.1mm2, adj f294
  f294: cylinder r=1.5mm len=29.1mm, axis (0,-1,0), area 274.3mm2, adj f292,f293
PLACE A rot(axis=(1,0,0),180deg) t=(0,-2.6,-0.52)mm
PLACE B at identity
MATE slider B.f290 <-> A.f12  axis (0,-1,0) through (0,0,0)mm
